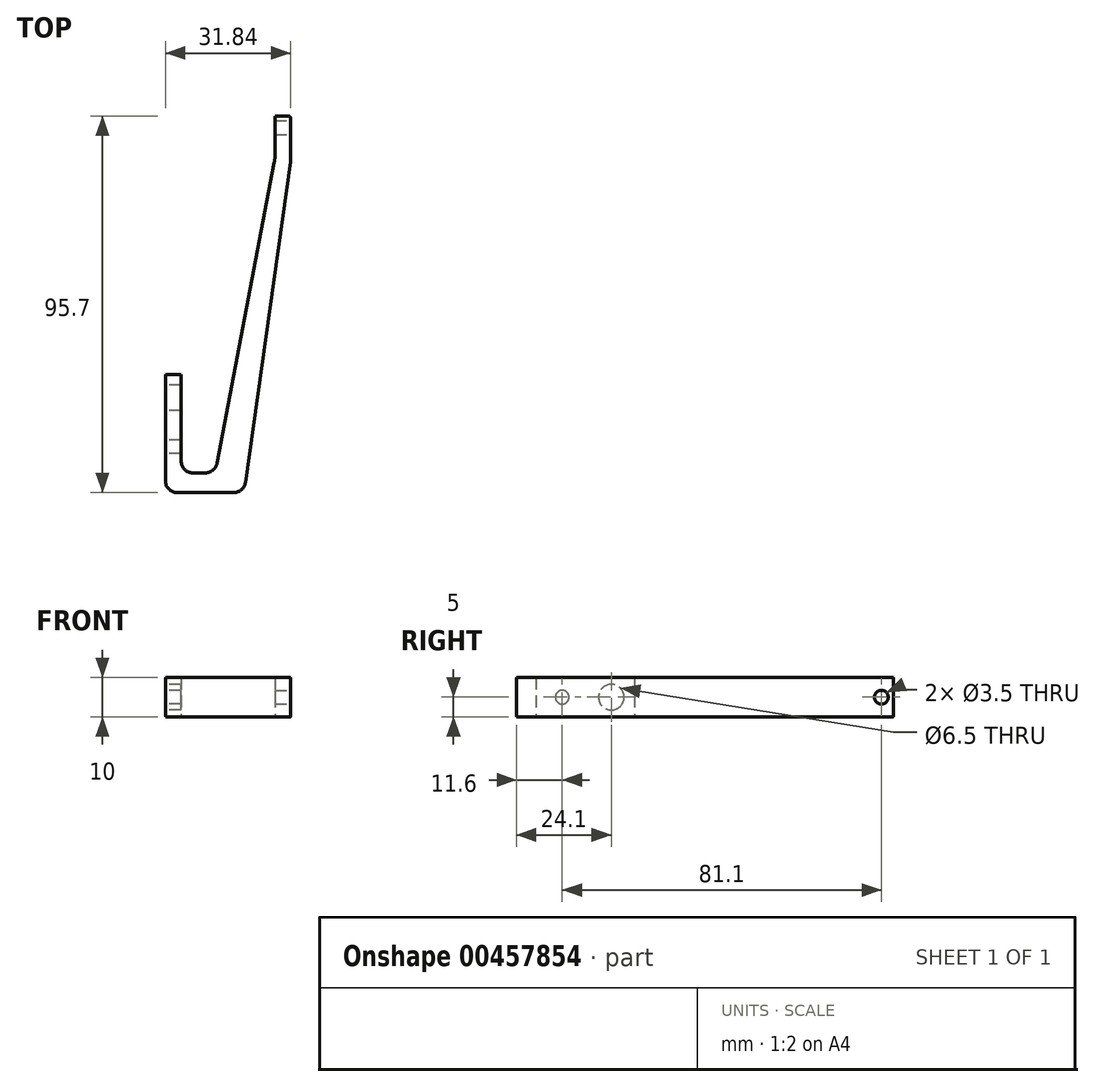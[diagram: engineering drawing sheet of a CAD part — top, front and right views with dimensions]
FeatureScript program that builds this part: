
annotation { "Feature Type Name" : "Feature", "Feature Type Description" : "" }
export const myFeature = defineFeature(function(context is Context, id is Id, definition is map)
    precondition{}
    {
        {
            var Q0;
            Q0=qCreatedBy(makeId("Top.planeOp"),FACE);
            var sketch = newSketch(context, id + "F0", { "sketchPlane" : qUnion([Q0])});
            skLineSegment(sketch, "E0", {"start": v(0, 0) * mm, "end": v(20, 0) * mm});
            skLineSegment(sketch, "E1.top", {"start": v(31.84, 95.7) * mm, "end": v(27.84, 95.7) * mm});
            skLineSegment(sketch, "E1.left", {"start": v(31.84, 84.7) * mm, "end": v(31.84, 95.7) * mm});
            skLineSegment(sketch, "E1.right", {"start": v(27.84, 84.7) * mm, "end": v(27.84, 95.7) * mm});
            skLineSegment(sketch, "E2.right", {"start": v(27.84, 84.7) * mm, "end": v(27.84, 84.7) * mm});
            skLineSegment(sketch, "E3.bottom", {"start": v(4, 5) * mm, "end": v(0, 5) * mm});
            skLineSegment(sketch, "E3.top", {"start": v(4, 30) * mm, "end": v(0, 30) * mm});
            skLineSegment(sketch, "E3.right", {"start": v(0, 5) * mm, "end": v(0, 30) * mm});
            skLineSegment(sketch, "E4", {"start": v(0, 5) * mm, "end": v(0, 0) * mm});
            skLineSegment(sketch, "E5", {"start": v(27.84, 84.7) * mm, "end": v(31.84, 84.7) * mm, "construction": true});
            skLineSegment(sketch, "E6", {"start": v(4, 30) * mm, "end": v(4, 5) * mm});
            skLineSegment(sketch, "E7", {"start": v(31.84, 84.7) * mm, "end": v(20, 0) * mm});
            skLineSegment(sketch, "E8", {"start": v(27.84, 84.7) * mm, "end": v(12.68, 5) * mm});
            skLineSegment(sketch, "E9", {"start": v(4, 5) * mm, "end": v(12.68, 5) * mm});
            skLineSegment(sketch, "E10", {"start": v(27.84, 89.7) * mm, "end": v(31.84, 89.7) * mm, "construction": true});
            skLineSegment(sketch, "E11", {"start": v(0, 5) * mm, "end": v(4, 5) * mm, "construction": true});
            skSolve(sketch);
        }
        {
            var Q0;
            {var subQ0=sQuery(id+"F0.wireOp",EDGE,"E3.right");Q0=makeQuery(id+"F0.imprint","IMPRINT",FACE,{"disambiguationData":[TD([[makeQuery(id+"F0.imprint","IMPRINT",EDGE,{"derivedFrom":subQ0}),-1.0]])]});}
            var Q1;
            Q1=makeQuery(id+"F0.imprint","IMPRINT",FACE,{"disambiguationData":[TD([[makeQuery(id+"F0.imprint","IMPRINT",EDGE,{"derivedFrom":sQuery(id+"F0.wireOp",EDGE,"E0")}),1.0]])]});
            extrude(context, id + "F1", {"entities" : qUnion([Q0, Q1]), "depth" : 10 * mm});
        }
        {
            var Q0;
            Q0=makeQuery(id+"F1.opExtrude","SWEPT_EDGE",EDGE,{"disambiguationData":[OSD([sQuery(id+"F0.wireOp",EDGE,"vQo4EyD8-J1S7-a0HB-uYFw-dzZPHnMh1mcb"),sQuery(id+"F0.wireOp",EDGE,"fKfWOtUt-9wTc-nL7O-PbCy-WxuiiFAzQuoH")])]});
            var Q1;
            Q1=makeQuery(id+"F1.opExtrude","SWEPT_EDGE",EDGE,{"disambiguationData":[OSD([sQuery(id+"F0.wireOp",EDGE,"E0"),sQuery(id+"F0.wireOp",EDGE,"vQo4EyD8-J1S7-a0HB-uYFw-dzZPHnMh1mcb")])]});
            var Q2;
            Q2=makeQuery(id+"F1.opExtrude","SWEPT_EDGE",EDGE,{"disambiguationData":[OSD([sQuery(id+"F0.wireOp",EDGE,"E8"),sQuery(id+"F0.wireOp",EDGE,"E9")])]});
            var Q3;
            Q3=makeQuery(id+"F1.opExtrude","SWEPT_EDGE",EDGE,{"disambiguationData":[OSD([sQuery(id+"F0.wireOp",EDGE,"E3.bottom"),sQuery(id+"F0.wireOp",EDGE,"E6"),sQuery(id+"F0.wireOp",EDGE,"E9")])]});
            fillet(context, id + "F2", {"entities" : qUnion([Q0, Q1, Q2, Q3]), "radius" : 3 * mm, "tangentPropagation" : true, "allowEdgeOverflow" : false});
        }
        {
            var Q0;
            Q0=makeQuery(id+"F1.opExtrude","SWEPT_EDGE",EDGE,{"disambiguationData":[OSD([sQuery(id+"F0.wireOp",EDGE,"E1.right"),sQuery(id+"F0.wireOp",EDGE,"E8")])]});
            var Q1;
            Q1=makeQuery(id+"F1.opExtrude","SWEPT_EDGE",EDGE,{"disambiguationData":[OSD([sQuery(id+"F0.wireOp",EDGE,"E1.left"),sQuery(id+"F0.wireOp",EDGE,"E7")])]});
            fillet(context, id + "F3", {"entities" : qUnion([Q0, Q1]), "radius" : 10 * mm, "tangentPropagation" : true, "allowEdgeOverflow" : false});
        }
        {
            var Q0;
            Q0=makeQuery(id+"F1.opExtrude","SWEPT_FACE",FACE,{"disambiguationData":[OSD([sQuery(id+"F0.wireOp",EDGE,"E1.left"),sQuery(id+"F0.wireOp",EDGE,"fKfWOtUt-9wTc-nL7O-PbCy-WxuiiFAzQuoH")])]});
            var sketch = newSketch(context, id + "F4", { "sketchPlane" : qUnion([Q0])});
            skCircle(sketch, "E12", {"center": v(92.7, 5) * mm, "radius": 1.75 * mm});
            skSolve(sketch);
        }
        {
            var Q0;
            Q0=makeQuery(id+"F4.imprint","IMPRINT",FACE,{"disambiguationData":[TD([[makeQuery(id+"F4.imprint","IMPRINT",EDGE,{"derivedFrom":sQuery(id+"F4.wireOp",EDGE,"E12")}),1.0]])]});
            extrude(context, id + "F5", {"entities" : qUnion([Q0]), "operationType" : NewBodyOperationType.REMOVE, "oppositeDirection" : true, "depth" : 5 * mm});
        }
        {
            var Q0;
            Q0=makeQuery(id+"F1.opExtrude","SWEPT_FACE",FACE,{"disambiguationData":[OSD([sQuery(id+"F0.wireOp",EDGE,"E3.right"),sQuery(id+"F0.wireOp",EDGE,"E4")])]});
            var sketch = newSketch(context, id + "F6", { "sketchPlane" : qUnion([Q0])});
            skCircle(sketch, "E13", {"center": v(-24.1, 5) * mm, "radius": 3.25 * mm});
            skCircle(sketch, "E14", {"center": v(-11.6, 5) * mm, "radius": 1.75 * mm});
            skSolve(sketch);
        }
        {
            var Q0;
            Q0=makeQuery(id+"F6.imprint","IMPRINT",FACE,{"disambiguationData":[TD([[makeQuery(id+"F6.imprint","IMPRINT",EDGE,{"derivedFrom":sQuery(id+"F6.wireOp",EDGE,"E13")}),1.0]])]});
            var Q1;
            Q1=makeQuery(id+"F6.imprint","IMPRINT",FACE,{"disambiguationData":[TD([[makeQuery(id+"F6.imprint","IMPRINT",EDGE,{"derivedFrom":sQuery(id+"F6.wireOp",EDGE,"E14")}),1.0]])]});
            extrude(context, id + "F7", {"entities" : qUnion([Q0, Q1]), "operationType" : NewBodyOperationType.REMOVE, "oppositeDirection" : true, "depth" : 6 * mm});
        }
        {
            var Q0;
            Q0=makeQuery(id+"F1.opExtrude","SWEPT_EDGE",EDGE,{"disambiguationData":[OSD([sQuery(id+"F0.wireOp",EDGE,"E1.top"),sQuery(id+"F0.wireOp",EDGE,"E1.left")])]});
            fillet(context, id + "F8", {"entities" : qUnion([Q0]), "radius" : 0.7 * mm, "tangentPropagation" : true, "allowEdgeOverflow" : false});
        }
    });
